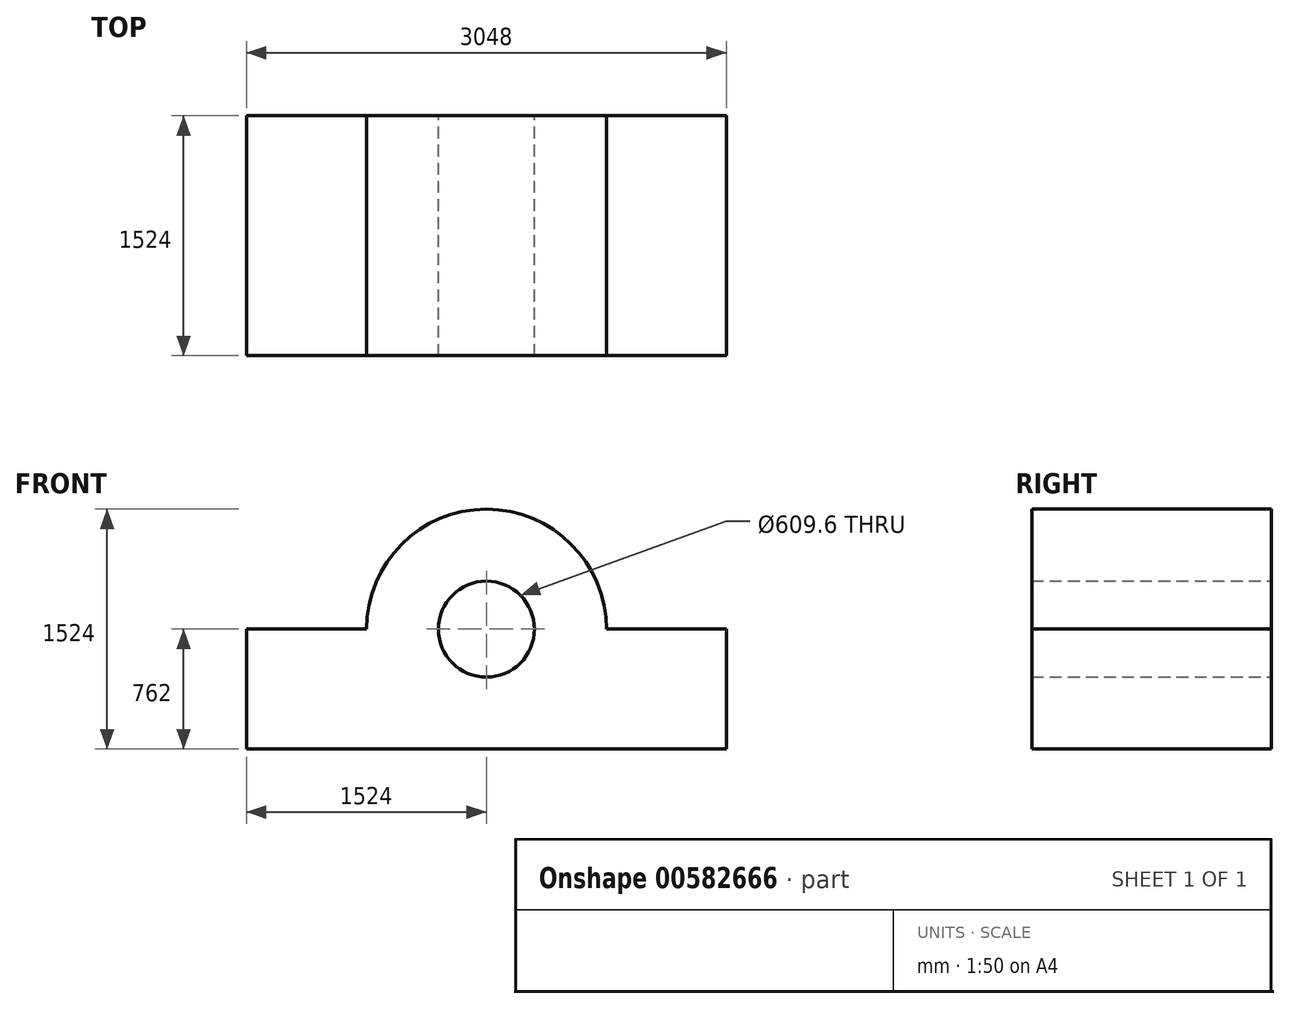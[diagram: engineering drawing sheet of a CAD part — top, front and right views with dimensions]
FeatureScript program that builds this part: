
annotation { "Feature Type Name" : "Feature", "Feature Type Description" : "" }
export const myFeature = defineFeature(function(context is Context, id is Id, definition is map)
    precondition{}
    {
        {
            var Q0;
            Q0=qCreatedBy(makeId("Front.planeOp"),FACE);
            var sketch = newSketch(context, id + "F0", { "sketchPlane" : qUnion([Q0])});
            skLineSegment(sketch, "E0", {"start": v(0, 0) * mm, "end": v(0, 762) * mm});
            skLineSegment(sketch, "E1", {"start": v(0, 0) * mm, "end": v(3048, 0) * mm});
            skLineSegment(sketch, "E2", {"start": v(3048, 0) * mm, "end": v(3048, 762) * mm});
            skPoint(sketch, "E3.centerSnap0", {"position": v(1524, 0) * mm});
            skArc(sketch, "E4", {"start": v(2286, 762) * mm, "mid": v(1524, 1524) * mm, "end": v(762, 762) * mm});
            skLineSegment(sketch, "E5", {"start": v(0, 762) * mm, "end": v(762, 762) * mm});
            skLineSegment(sketch, "E6", {"start": v(3048, 762) * mm, "end": v(2286, 762) * mm});
            skCircle(sketch, "E7", {"center": v(1524, 762) * mm, "radius": 304.8 * mm});
            skSolve(sketch);
        }
        {
            var Q0;
            Q0=makeQuery(id+"F0.imprint","IMPRINT",FACE,{"disambiguationData":[TD([[makeQuery(id+"F0.imprint","IMPRINT",EDGE,{"derivedFrom":sQuery(id+"F0.wireOp",EDGE,"E0")}),-1.0]])]});
            extrude(context, id + "F1", {"entities" : qUnion([Q0]), "depth" : 1524 * mm, "offsetDistance" : 25.4 * mm});
        }
    });
